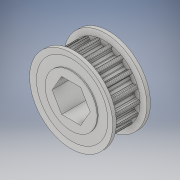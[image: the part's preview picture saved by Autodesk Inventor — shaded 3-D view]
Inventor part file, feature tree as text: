
AUTODESK INVENTOR PART (.ipt)
format: ipt  version: 2019 (Build 230136000, 136)  size: 511,488 bytes
history: native  units: in
note: dims shown in document units (in); Inventor stores cm internally (conversion verified against a paired STEP export)
features: mirror x1
ambient origin geometry x8: Origin, YZ Plane, XZ Plane, XY Plane, X Axis, Y Axis, Z Axis, Center Point
bodies: Solid1 (feature_tree)
feature tree (1):
  mirror  "Mirror1"
